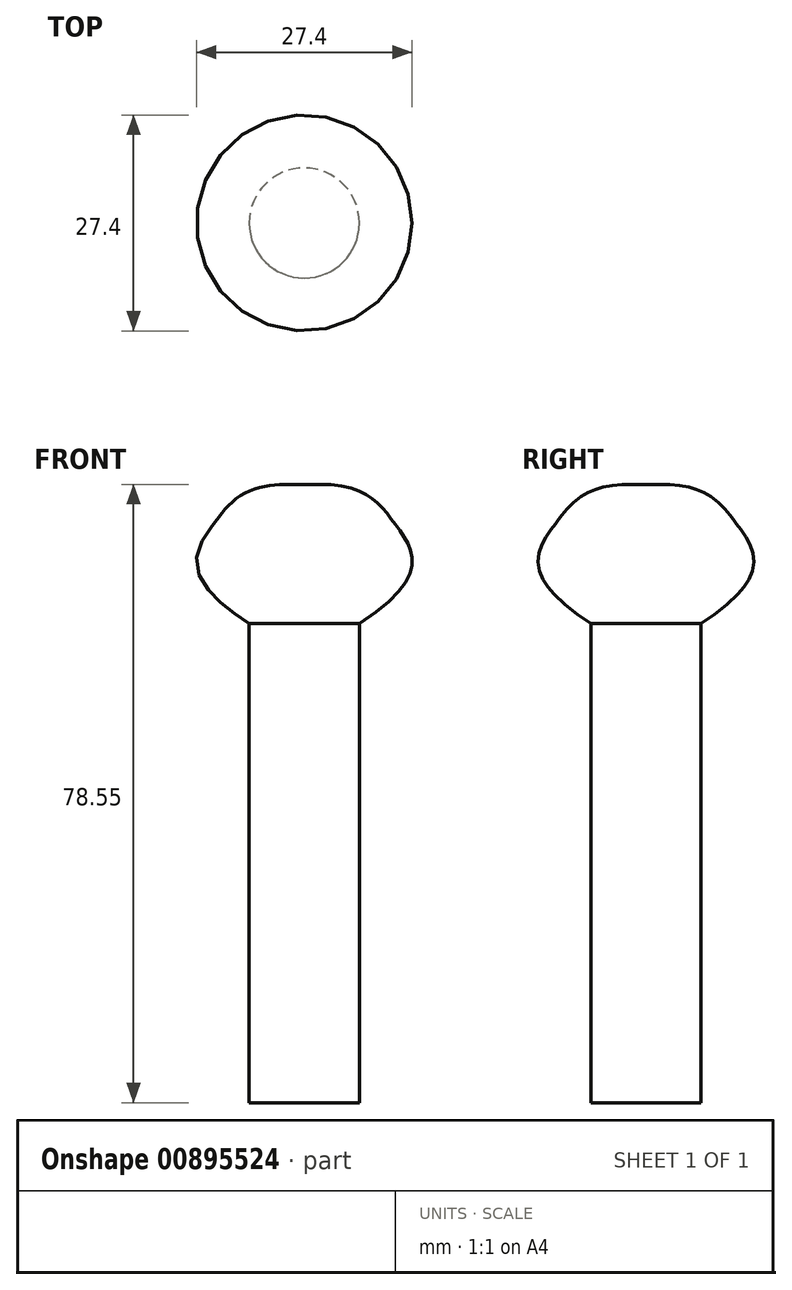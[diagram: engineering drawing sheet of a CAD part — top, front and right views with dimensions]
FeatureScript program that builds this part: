
annotation { "Feature Type Name" : "Feature", "Feature Type Description" : "" }
export const myFeature = defineFeature(function(context is Context, id is Id, definition is map)
    precondition{}
    {
        {
            var Q0;
            Q0=qCreatedBy(makeId("Front.planeOp"),FACE);
            var sketch = newSketch(context, id + "F0", { "sketchPlane" : qUnion([Q0])});
            skLineSegment(sketch, "E0", {"start": v(0, 0) * mm, "end": v(0, 72.02) * mm, "construction": true});
            skLineSegment(sketch, "E1", {"start": v(0, 0) * mm, "end": v(7, 0) * mm});
            skLineSegment(sketch, "E2", {"start": v(7, 0) * mm, "end": v(7, 60.88) * mm});
            skFitSpline(sketch, "E3", {"points": [v(7, 60.88) * mm, v(11.45, 73.62) * mm, v(0, 78.5) * mm], "startDerivative": vector(56.37, 35.74) * mm, "endDerivative": vector(-46.15, -2.96) * mm});
            skSolve(sketch);
        }
        {
            var Q0;
            Q0=qCreatedBy(makeId("Front.planeOp"),FACE);
            var sketch = newSketch(context, id + "F1", { "sketchPlane" : qUnion([Q0])});
            skLineSegment(sketch, "E4", {"start": v(0, 47.36) * mm, "end": v(0, 0) * mm, "construction": true});
            skSolve(sketch);
        }
        {
            var Q0;
            Q0 = qConstructionFilter(qBodyType(qCreatedBy(id + "F0" ,EDGE), BodyType.WIRE), ConstructionObject.NO);
            var Q1;
            Q1=sQuery(id+"F1.wireOp",EDGE,"E4");
            revolve(context, id + "F2", {"bodyType" : ToolBodyType.SURFACE, "surfaceOperationType" : NewSurfaceOperationType.NEW, "surfaceEntities" : qUnion([Q0]), "axis" : qUnion([Q1]), "revolveType" : RevolveType.FULL});
        }
    });
